# Revit family: CLH
name_source: partatom
category: Lighting Fixtures
revit_build: Autodesk Revit 2013 (Build: 20130531_2115(x64)
units: mm (PartAtom-declared; Revit-internal decimal feet)

## types (4) — shared parameters
Apparent Load = 218 VA
Color Filter = 16777215
Default Elevation = 48 "
Description = Sealed LED fixture for hazardous locations
Dimming = Non-Dimming
Dimming Lamp Color Temperature Shift = <None>
Emit Shape Visible in Rendering = No
Emit from Circle Diameter = 15 "
Lamp = Smooth high output LED light fixture
Light Bulb Material = Hubbell - White Glass
Load Classification = Lighting
Manufacturer = Hubbell Industrial Lighting
Manufacturer Fax = 866-898-0131
Model = CHL
Mounting = Pendant
Pendant Height = 36 "
Power Factor = 1
Product Documentation Link = http://cdn.hubbellindustrial.com
Product Material = Power Coat - Hubbell - White
Product Page URL = http://www.hubbellindustrial.com
Tilt Angle = -90.00°
URL = http://www.hubbellindustrial.com
Voltage = 120 V
Warranty = Five years warranty
Wattage Comments = Up to 24,000 lumens, 113 LPW and 220 total watts
Watts = 218 W

## per-type parameters (varying)
| type | Lens | Lens Type | Photometric Web File |
| CLH-5K-SPC | Sag Polycarbonate | Lens : SPC | IES_FPH-5K-SPC-U-ND-A2-WH_14.00862.ies |
| CLH-5K-P95 | Acrylic P95 | Lens : P95 | IES_FPH-5K-P95-U-ND-A2-WH_15.00001.ies |
| CLH-5K-DLR | Prismatic Drop Acrylic | Lens : DLR | IES_FPH-5K-DLR-U-ND-A2-WH_14.00863.ies |
| CLH-5K-CDL | Prismatic Conical Drop Acrylic | Lens : CDL | IES_FPH-5K-CDL-U-ND-A2-WH_14.00864.ies |

## geometry (parser evidence)
native form markers: Sweep x6
no freeform markers — native parametric forms only
